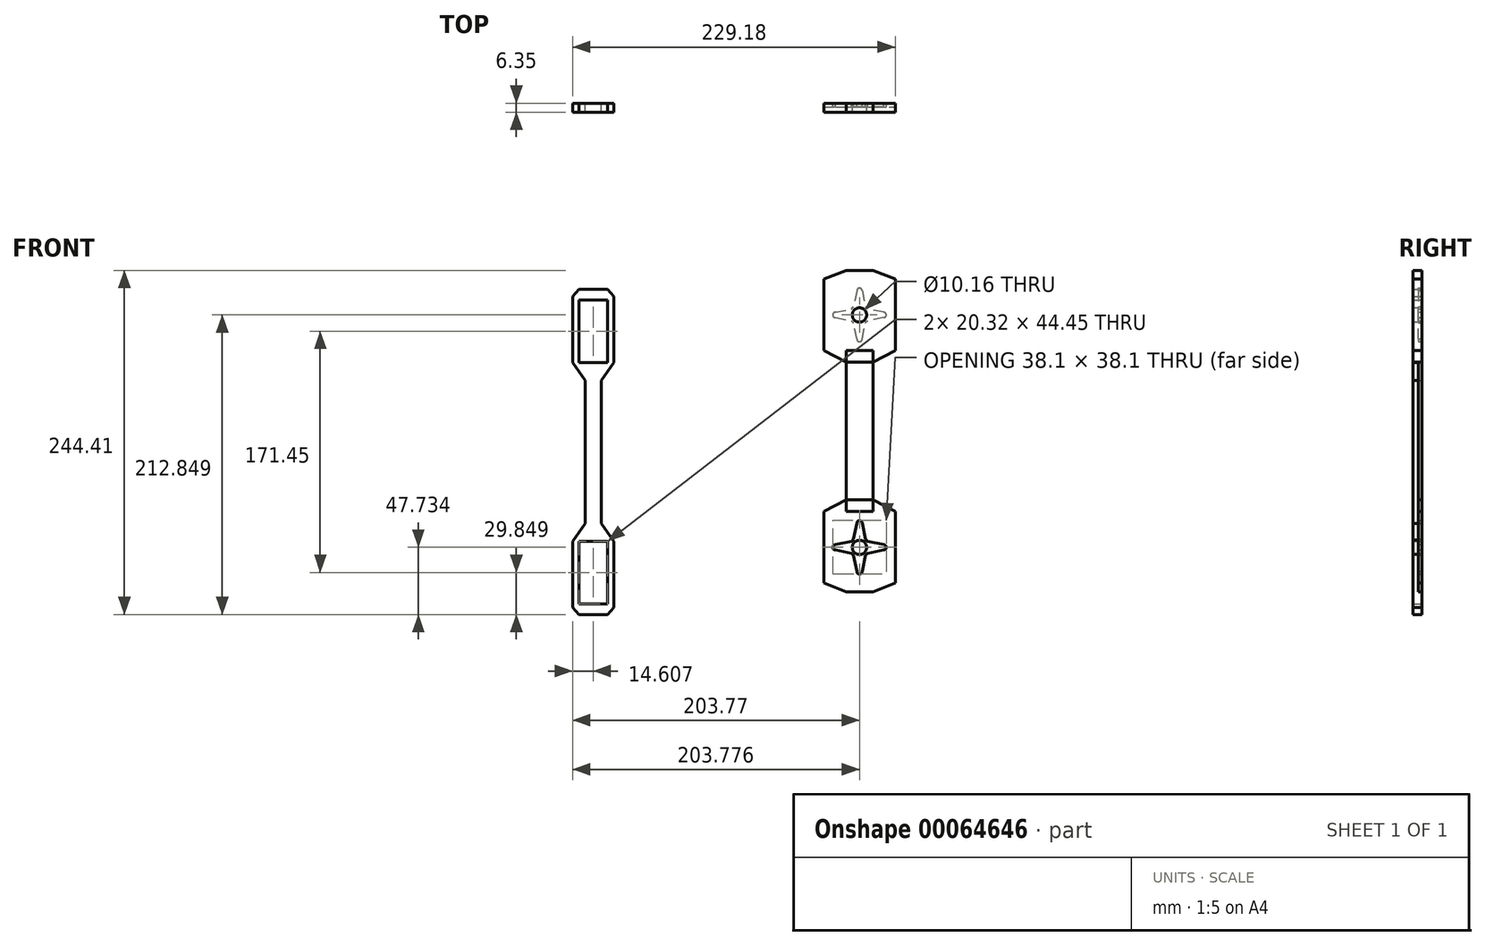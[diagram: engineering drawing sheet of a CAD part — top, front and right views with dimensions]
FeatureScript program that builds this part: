
annotation { "Feature Type Name" : "Feature", "Feature Type Description" : "" }
export const myFeature = defineFeature(function(context is Context, id is Id, definition is map)
    precondition{}
    {
        {
            var Q0;
            Q0=qCreatedBy(makeId("Front.planeOp"),FACE);
            var sketch = newSketch(context, id + "F0", { "sketchPlane" : qUnion([Q0])});
            skLineSegment(sketch, "E0.bottom", {"start": v(-81.1, 17.43) * mm, "end": v(-69.67, 17.43) * mm});
            skLineSegment(sketch, "E0.top", {"start": v(-81.1, -46.07) * mm, "end": v(-69.67, -46.07) * mm});
            skLineSegment(sketch, "E0.left", {"start": v(-81.1, 17.43) * mm, "end": v(-81.1, -46.07) * mm});
            skLineSegment(sketch, "E0.right", {"start": v(-69.67, 17.43) * mm, "end": v(-69.67, -46.07) * mm});
            skLineSegment(sketch, "E1.bottom", {"start": v(-89.99, 17.43) * mm, "end": v(-60.78, 17.43) * mm});
            skLineSegment(sketch, "E1.top", {"start": v(-89.99, 64.42) * mm, "end": v(-60.78, 64.42) * mm});
            skLineSegment(sketch, "E1.left", {"start": v(-89.99, 17.43) * mm, "end": v(-89.99, 64.42) * mm});
            skLineSegment(sketch, "E1.right", {"start": v(-60.78, 17.43) * mm, "end": v(-60.78, 64.42) * mm});
            skLineSegment(sketch, "E2", {"start": v(-81.1, 4.73) * mm, "end": v(-89.99, 17.43) * mm});
            skLineSegment(sketch, "E3", {"start": v(-69.67, 4.73) * mm, "end": v(-60.78, 17.43) * mm});
            skLineSegment(sketch, "E4.bottom", {"start": v(-85.54, 17.43) * mm, "end": v(-65.22, 17.43) * mm});
            skLineSegment(sketch, "E4.top", {"start": v(-85.54, 61.88) * mm, "end": v(-65.22, 61.88) * mm});
            skLineSegment(sketch, "E4.left", {"start": v(-85.54, 17.43) * mm, "end": v(-85.54, 61.88) * mm});
            skLineSegment(sketch, "E4.right", {"start": v(-65.22, 17.43) * mm, "end": v(-65.22, 61.88) * mm});
            skLineSegment(sketch, "E5.MirrorCS", {"start": v(-81.1, -109.57) * mm, "end": v(-69.67, -109.57) * mm});
            skLineSegment(sketch, "E6.MirrorCS", {"start": v(-81.1, -109.57) * mm, "end": v(-81.1, -46.07) * mm});
            skLineSegment(sketch, "E7.MirrorCS", {"start": v(-69.67, -109.57) * mm, "end": v(-69.67, -46.07) * mm});
            skLineSegment(sketch, "E8.MirrorCS", {"start": v(-89.99, -109.57) * mm, "end": v(-60.78, -109.57) * mm});
            skLineSegment(sketch, "E9.MirrorCS", {"start": v(-89.99, -156.56) * mm, "end": v(-60.78, -156.56) * mm});
            skLineSegment(sketch, "E10.MirrorCS", {"start": v(-89.99, -109.57) * mm, "end": v(-89.99, -156.56) * mm});
            skLineSegment(sketch, "E11.MirrorCS", {"start": v(-60.78, -109.57) * mm, "end": v(-60.78, -156.56) * mm});
            skLineSegment(sketch, "E12.MirrorCS", {"start": v(-81.1, -96.87) * mm, "end": v(-89.99, -109.57) * mm});
            skLineSegment(sketch, "E13.MirrorCS", {"start": v(-69.67, -96.87) * mm, "end": v(-60.78, -109.57) * mm});
            skLineSegment(sketch, "E14.MirrorCS", {"start": v(-65.22, -109.57) * mm, "end": v(-65.22, -154.02) * mm});
            skLineSegment(sketch, "E15.MirrorCS", {"start": v(-85.54, -109.57) * mm, "end": v(-85.54, -154.02) * mm});
            skLineSegment(sketch, "E16.MirrorCS", {"start": v(-85.54, -154.02) * mm, "end": v(-65.22, -154.02) * mm});
            skLineSegment(sketch, "E17.MirrorCS", {"start": v(-85.54, -109.57) * mm, "end": v(-65.22, -109.57) * mm});
            skLineSegment(sketch, "E18", {"start": v(-89.99, 64.42) * mm, "end": v(-85.54, 69.5) * mm});
            skLineSegment(sketch, "E19", {"start": v(-85.54, 69.5) * mm, "end": v(-65.22, 69.5) * mm});
            skLineSegment(sketch, "E20", {"start": v(-65.22, 69.5) * mm, "end": v(-60.78, 64.42) * mm});
            skLineSegment(sketch, "E21.MirrorCS", {"start": v(-85.54, -161.64) * mm, "end": v(-65.22, -161.64) * mm});
            skLineSegment(sketch, "E22.MirrorCS", {"start": v(-89.99, -156.56) * mm, "end": v(-85.54, -161.64) * mm});
            skLineSegment(sketch, "E23.MirrorCS", {"start": v(-65.22, -161.64) * mm, "end": v(-60.78, -156.56) * mm});
            skSolve(sketch);
        }
        {
            var Q0;
            Q0=makeQuery(id+"F0.imprint","IMPRINT",FACE,{"disambiguationData":[TD([[makeQuery(id+"F0.imprint","IMPRINT",EDGE,{"derivedFrom":sQuery(id+"F0.wireOp",EDGE,"E1.top")}),-1.0]])]});
            var Q1;
            {var subQ3=sQuery(id+"F0.wireOp",EDGE,"E2");Q1=makeQuery(id+"F0.imprint","IMPRINT",FACE,{"disambiguationData":[TD([[makeQuery(id+"F0.imprint","IMPRINT",EDGE,{"derivedFrom":subQ3}),-1.0]])]});}
            var Q2;
            {var subQ5=sQuery(id+"F0.wireOp",EDGE,"E0.top");Q2=makeQuery(id+"F0.imprint","IMPRINT",FACE,{"disambiguationData":[TD([[makeQuery(id+"F0.imprint","IMPRINT",EDGE,{"derivedFrom":subQ5}),1.0]])]});}
            var Q3;
            {var subQ3=sQuery(id+"F0.wireOp",EDGE,"E3");Q3=makeQuery(id+"F0.imprint","IMPRINT",FACE,{"disambiguationData":[TD([[makeQuery(id+"F0.imprint","IMPRINT",EDGE,{"derivedFrom":subQ3}),1.0]])]});}
            var Q4;
            {var subQ5=sQuery(id+"F0.wireOp",EDGE,"E0.top");Q4=makeQuery(id+"F0.imprint","IMPRINT",FACE,{"disambiguationData":[TD([[makeQuery(id+"F0.imprint","IMPRINT",EDGE,{"derivedFrom":subQ5}),-1.0]])]});}
            var Q5;
            {var subQ3=sQuery(id+"F0.wireOp",EDGE,"E12.MirrorCS");Q5=makeQuery(id+"F0.imprint","IMPRINT",FACE,{"disambiguationData":[TD([[makeQuery(id+"F0.imprint","IMPRINT",EDGE,{"derivedFrom":subQ3}),1.0]])]});}
            var Q6;
            {var subQ3=sQuery(id+"F0.wireOp",EDGE,"E13.MirrorCS");Q6=makeQuery(id+"F0.imprint","IMPRINT",FACE,{"disambiguationData":[TD([[makeQuery(id+"F0.imprint","IMPRINT",EDGE,{"derivedFrom":subQ3}),-1.0]])]});}
            var Q7;
            Q7=makeQuery(id+"F0.imprint","IMPRINT",FACE,{"disambiguationData":[TD([[makeQuery(id+"F0.imprint","IMPRINT",EDGE,{"derivedFrom":sQuery(id+"F0.wireOp",EDGE,"E9.MirrorCS")}),1.0]])]});
            var Q8;
            Q8=makeQuery(id+"F0.imprint","IMPRINT",FACE,{"disambiguationData":[TD([[makeQuery(id+"F0.imprint","IMPRINT",EDGE,{"derivedFrom":sQuery(id+"F0.wireOp",EDGE,"E1.top")}),1.0]])]});
            var Q9;
            Q9=makeQuery(id+"F0.imprint","IMPRINT",FACE,{"disambiguationData":[TD([[makeQuery(id+"F0.imprint","IMPRINT",EDGE,{"derivedFrom":sQuery(id+"F0.wireOp",EDGE,"E9.MirrorCS")}),-1.0]])]});
            extrude(context, id + "F1", {"entities" : qUnion([Q0, Q1, Q2, Q3, Q4, Q5, Q6, Q7, Q8, Q9]), "depth" : 6.35 * mm});
        }
        {
            var Q0;
            Q0=qCreatedBy(makeId("Front.planeOp"),FACE);
            var sketch = newSketch(context, id + "F2", { "sketchPlane" : qUnion([Q0])});
            skLineSegment(sketch, "E24.bottom", {"start": v(88.39, 76.6) * mm, "end": v(139.19, 76.6) * mm});
            skLineSegment(sketch, "E24.top", {"start": v(88.39, 25.8) * mm, "end": v(139.19, 25.8) * mm});
            skLineSegment(sketch, "E24.left", {"start": v(88.39, 76.6) * mm, "end": v(88.39, 25.8) * mm});
            skLineSegment(sketch, "E24.right", {"start": v(139.19, 76.6) * mm, "end": v(139.19, 25.8) * mm});
            skLineSegment(sketch, "E25.bottom", {"start": v(104.26, -31.36) * mm, "end": v(123.31, -31.36) * mm});
            skLineSegment(sketch, "E25.top", {"start": v(104.26, 25.8) * mm, "end": v(123.31, 25.8) * mm});
            skLineSegment(sketch, "E25.left", {"start": v(104.26, -31.36) * mm, "end": v(104.26, 25.8) * mm});
            skLineSegment(sketch, "E25.right", {"start": v(123.31, -31.36) * mm, "end": v(123.31, 25.8) * mm});
            skLineSegment(sketch, "E26", {"start": v(88.39, 25.8) * mm, "end": v(104.26, 17.53) * mm});
            skLineSegment(sketch, "E27", {"start": v(104.26, 17.53) * mm, "end": v(123.31, 17.53) * mm});
            skLineSegment(sketch, "E28", {"start": v(123.31, 17.53) * mm, "end": v(139.19, 25.8) * mm});
            skLineSegment(sketch, "E29", {"start": v(88.39, 76.6) * mm, "end": v(104.26, 82.77) * mm});
            skLineSegment(sketch, "E30", {"start": v(104.26, 82.77) * mm, "end": v(123.31, 82.77) * mm});
            skLineSegment(sketch, "E31", {"start": v(123.31, 82.77) * mm, "end": v(139.19, 76.6) * mm});
            skLineSegment(sketch, "E32", {"start": v(113.79, 51.2) * mm, "end": v(113.79, 70.24) * mm});
            skPoint(sketch, "E32.startSnap0", {"position": v(113.79, 76.6) * mm});
            skPoint(sketch, "E32.startSnap1", {"position": v(88.39, 51.2) * mm});
            skCircle(sketch, "E33", {"center": v(113.79, 68.34) * mm, "radius": 1.9 * mm});
            skCircle(sketch, "E34", {"center": v(113.79, 51.2) * mm, "radius": 4.86 * mm});
            skLineSegment(sketch, "E35", {"start": v(113.79, 51.2) * mm, "end": v(110.35, 54.63) * mm});
            skLineSegment(sketch, "E36", {"start": v(110.35, 54.63) * mm, "end": v(111.88, 68.34) * mm});
            skLineSegment(sketch, "E37.MirrorCS", {"start": v(117.23, 54.63) * mm, "end": v(115.7, 68.34) * mm});
            skLineSegment(sketch, "E38", {"start": v(111.88, 68.34) * mm, "end": v(109.47, 56.89) * mm});
            skLineSegment(sketch, "E39.MirrorCS", {"start": v(115.7, 68.34) * mm, "end": v(118.1, 56.89) * mm});
            skLineSegment(sketch, "E40.1.0", {"start": v(96.64, 53.1) * mm, "end": v(108.1, 55.51) * mm});
            skLineSegment(sketch, "E40.1.1", {"start": v(96.64, 49.29) * mm, "end": v(108.1, 46.88) * mm});
            skCircle(sketch, "E40.1.2", {"center": v(96.64, 51.2) * mm, "radius": 1.9 * mm});
            skLineSegment(sketch, "E40.1.3", {"start": v(113.79, 51.2) * mm, "end": v(94.74, 51.2) * mm});
            skLineSegment(sketch, "E40.2.0", {"start": v(111.88, 34.05) * mm, "end": v(109.47, 45.5) * mm});
            skLineSegment(sketch, "E40.2.1", {"start": v(115.7, 34.05) * mm, "end": v(118.1, 45.5) * mm});
            skCircle(sketch, "E40.2.2", {"center": v(113.79, 34.05) * mm, "radius": 1.9 * mm});
            skLineSegment(sketch, "E40.2.3", {"start": v(113.79, 51.2) * mm, "end": v(113.79, 32.14) * mm});
            skLineSegment(sketch, "E40.3.0", {"start": v(130.93, 49.29) * mm, "end": v(119.48, 46.88) * mm});
            skLineSegment(sketch, "E40.3.1", {"start": v(130.93, 53.1) * mm, "end": v(119.48, 55.51) * mm});
            skCircle(sketch, "E40.3.2", {"center": v(130.93, 51.2) * mm, "radius": 1.9 * mm});
            skLineSegment(sketch, "E40.3.3", {"start": v(113.79, 51.2) * mm, "end": v(132.84, 51.2) * mm});
            skLineSegment(sketch, "E41", {"start": v(108.1, 55.51) * mm, "end": v(109.47, 56.89) * mm});
            skLineSegment(sketch, "E42", {"start": v(118.1, 56.89) * mm, "end": v(119.48, 55.51) * mm});
            skLineSegment(sketch, "E43", {"start": v(119.48, 46.88) * mm, "end": v(118.1, 45.5) * mm});
            skLineSegment(sketch, "E44", {"start": v(109.47, 45.5) * mm, "end": v(108.1, 46.88) * mm});
            skLineSegment(sketch, "E45.MirrorCS", {"start": v(113.79, -113.9) * mm, "end": v(110.35, -117.34) * mm});
            skLineSegment(sketch, "E46.MirrorCS", {"start": v(108.1, -118.22) * mm, "end": v(109.47, -119.6) * mm});
            skCircle(sketch, "E47.MirrorC", {"center": v(113.79, -131.05) * mm, "radius": 1.9 * mm});
            skCircle(sketch, "E48.MirrorC", {"center": v(130.93, -113.9) * mm, "radius": 1.9 * mm});
            skLineSegment(sketch, "E49.MirrorCS", {"start": v(109.47, -108.21) * mm, "end": v(108.1, -109.59) * mm});
            skCircle(sketch, "E50.MirrorC", {"center": v(113.79, -113.9) * mm, "radius": 4.86 * mm});
            skLineSegment(sketch, "E51.MirrorCS", {"start": v(111.88, -131.05) * mm, "end": v(109.47, -119.6) * mm});
            skCircle(sketch, "E52.MirrorC", {"center": v(113.79, -96.76) * mm, "radius": 1.9 * mm});
            skLineSegment(sketch, "E53.MirrorCS", {"start": v(118.1, -119.6) * mm, "end": v(119.48, -118.22) * mm});
            skLineSegment(sketch, "E54.MirrorCS", {"start": v(119.48, -109.59) * mm, "end": v(118.1, -108.21) * mm});
            skLineSegment(sketch, "E55.MirrorCS", {"start": v(115.7, -131.05) * mm, "end": v(118.1, -119.6) * mm});
            skLineSegment(sketch, "E56.MirrorCS", {"start": v(113.79, -113.9) * mm, "end": v(113.79, -132.96) * mm});
            skLineSegment(sketch, "E57.MirrorCS", {"start": v(110.35, -117.34) * mm, "end": v(111.88, -131.05) * mm});
            skCircle(sketch, "E58.MirrorC", {"center": v(96.64, -113.9) * mm, "radius": 1.9 * mm});
            skLineSegment(sketch, "E59.MirrorCS", {"start": v(88.39, -88.5) * mm, "end": v(104.26, -80.24) * mm});
            skLineSegment(sketch, "E60.MirrorCS", {"start": v(115.7, -96.76) * mm, "end": v(118.1, -108.21) * mm});
            skLineSegment(sketch, "E61.MirrorCS", {"start": v(96.64, -112) * mm, "end": v(108.1, -109.59) * mm});
            skLineSegment(sketch, "E62.MirrorCS", {"start": v(123.31, -31.36) * mm, "end": v(123.31, -88.5) * mm});
            skLineSegment(sketch, "E63.MirrorCS", {"start": v(88.39, -139.3) * mm, "end": v(88.39, -88.5) * mm});
            skLineSegment(sketch, "E64.MirrorCS", {"start": v(130.93, -112) * mm, "end": v(119.48, -109.59) * mm});
            skLineSegment(sketch, "E65.MirrorCS", {"start": v(88.39, -139.3) * mm, "end": v(139.19, -139.3) * mm});
            skLineSegment(sketch, "E66.MirrorCS", {"start": v(104.26, -145.48) * mm, "end": v(123.31, -145.48) * mm});
            skLineSegment(sketch, "E67.MirrorCS", {"start": v(88.39, -88.5) * mm, "end": v(139.19, -88.5) * mm});
            skLineSegment(sketch, "E68.MirrorCS", {"start": v(113.79, -113.9) * mm, "end": v(94.74, -113.9) * mm});
            skLineSegment(sketch, "E69.MirrorCS", {"start": v(104.26, -31.36) * mm, "end": v(104.26, -88.5) * mm});
            skPoint(sketch, "E70.MirrorP", {"position": v(113.79, -139.3) * mm});
            skLineSegment(sketch, "E71.MirrorCS", {"start": v(113.79, -113.9) * mm, "end": v(132.84, -113.9) * mm});
            skLineSegment(sketch, "E72.MirrorCS", {"start": v(96.64, -115.81) * mm, "end": v(108.1, -118.22) * mm});
            skLineSegment(sketch, "E73.MirrorCS", {"start": v(130.93, -115.81) * mm, "end": v(119.48, -118.22) * mm});
            skPoint(sketch, "E74.MirrorP", {"position": v(88.39, -113.9) * mm});
            skLineSegment(sketch, "E75.MirrorCS", {"start": v(111.88, -96.76) * mm, "end": v(109.47, -108.21) * mm});
            skLineSegment(sketch, "E76.MirrorCS", {"start": v(113.79, -113.9) * mm, "end": v(113.79, -94.86) * mm});
            skLineSegment(sketch, "E77.MirrorCS", {"start": v(117.23, -117.34) * mm, "end": v(115.7, -131.05) * mm});
            skLineSegment(sketch, "E78.MirrorCS", {"start": v(139.19, -139.3) * mm, "end": v(139.19, -88.5) * mm});
            skLineSegment(sketch, "E79.MirrorCS", {"start": v(88.39, -139.3) * mm, "end": v(104.26, -145.48) * mm});
            skLineSegment(sketch, "E80.MirrorCS", {"start": v(123.31, -80.24) * mm, "end": v(139.19, -88.5) * mm});
            skLineSegment(sketch, "E81.MirrorCS", {"start": v(123.31, -145.48) * mm, "end": v(139.19, -139.3) * mm});
            skLineSegment(sketch, "E82.MirrorCS", {"start": v(104.26, -88.5) * mm, "end": v(123.31, -88.5) * mm});
            skLineSegment(sketch, "E83.MirrorCS", {"start": v(104.26, -80.24) * mm, "end": v(123.31, -80.24) * mm});
            skSolve(sketch);
        }
        {
            var Q0;
            Q0=makeQuery(id+"F2.imprint","IMPRINT",FACE,{"disambiguationData":[TD([[makeQuery(id+"F2.imprint","IMPRINT",EDGE,{"derivedFrom":sQuery(id+"F2.wireOp",EDGE,"E46.MirrorCS")}),-1.0]])]});
            var Q1;
            Q1=makeQuery(id+"F2.imprint","IMPRINT",FACE,{"disambiguationData":[TD([[makeQuery(id+"F2.imprint","IMPRINT",EDGE,{"derivedFrom":sQuery(id+"F2.wireOp",EDGE,"E65.MirrorCS")}),-1.0]])]});
            var Q2;
            {var subQ0=sQuery(id+"F2.wireOp",EDGE,"E59.MirrorCS");Q2=makeQuery(id+"F2.imprint","IMPRINT",FACE,{"disambiguationData":[TD([[makeQuery(id+"F2.imprint","IMPRINT",EDGE,{"derivedFrom":subQ0}),-1.0]])]});}
            var Q3;
            {var subQ0=sQuery(id+"F2.wireOp",EDGE,"E82.MirrorCS");Q3=makeQuery(id+"F2.imprint","IMPRINT",FACE,{"disambiguationData":[TD([[makeQuery(id+"F2.imprint","IMPRINT",EDGE,{"derivedFrom":subQ0}),1.0]])]});}
            var Q4;
            {var subQ3=sQuery(id+"F2.wireOp",EDGE,"E80.MirrorCS");Q4=makeQuery(id+"F2.imprint","IMPRINT",FACE,{"disambiguationData":[TD([[makeQuery(id+"F2.imprint","IMPRINT",EDGE,{"derivedFrom":subQ3}),-1.0]])]});}
            var Q5;
            {var subQ0=sQuery(id+"F2.wireOp",EDGE,"E25.bottom");Q5=makeQuery(id+"F2.imprint","IMPRINT",FACE,{"disambiguationData":[TD([[makeQuery(id+"F2.imprint","IMPRINT",EDGE,{"derivedFrom":subQ0}),-1.0]])]});}
            var Q6;
            {var subQ0=sQuery(id+"F2.wireOp",EDGE,"E25.bottom");Q6=makeQuery(id+"F2.imprint","IMPRINT",FACE,{"disambiguationData":[TD([[makeQuery(id+"F2.imprint","IMPRINT",EDGE,{"derivedFrom":subQ0}),1.0]])]});}
            var Q7;
            Q7=makeQuery(id+"F2.imprint","IMPRINT",FACE,{"disambiguationData":[TD([[makeQuery(id+"F2.imprint","IMPRINT",EDGE,{"derivedFrom":sQuery(id+"F2.wireOp",EDGE,"E24.bottom")}),-1.0]])]});
            var Q8;
            {var subQ0=sQuery(id+"F2.wireOp",EDGE,"E26");Q8=makeQuery(id+"F2.imprint","IMPRINT",FACE,{"disambiguationData":[TD([[makeQuery(id+"F2.imprint","IMPRINT",EDGE,{"derivedFrom":subQ0}),1.0]])]});}
            var Q9;
            {var subQ0=sQuery(id+"F2.wireOp",EDGE,"E25.top");Q9=makeQuery(id+"F2.imprint","IMPRINT",FACE,{"disambiguationData":[TD([[makeQuery(id+"F2.imprint","IMPRINT",EDGE,{"derivedFrom":subQ0}),-1.0]])]});}
            var Q10;
            {var subQ0=sQuery(id+"F2.wireOp",EDGE,"E28");Q10=makeQuery(id+"F2.imprint","IMPRINT",FACE,{"disambiguationData":[TD([[makeQuery(id+"F2.imprint","IMPRINT",EDGE,{"derivedFrom":subQ0}),1.0]])]});}
            var Q11;
            Q11=makeQuery(id+"F2.imprint","IMPRINT",FACE,{"disambiguationData":[TD([[makeQuery(id+"F2.imprint","IMPRINT",EDGE,{"derivedFrom":sQuery(id+"F2.wireOp",EDGE,"E24.bottom")}),1.0]])]});
            var Q12;
            Q12 = qSketchRegion(id + "F4", true);
            extrude(context, id + "F3", {"entities" : qUnion([Q0, Q1, Q2, Q3, Q4, Q5, Q6, Q7, Q8, Q9, Q10, Q11, Q12]), "depth" : 2.54 * mm});
        }
        {
            var Q0;
            Q0=makeQuery(id+"F3.opExtrude","CAP_FACE",FACE,{"disambiguationData":[OSD([sQuery(id+"F2.wireOp",EDGE,"E24.left"),sQuery(id+"F2.wireOp",EDGE,"E24.right"),sQuery(id+"F2.wireOp",EDGE,"E25.left"),sQuery(id+"F2.wireOp",EDGE,"E25.right"),sQuery(id+"F2.wireOp",EDGE,"E26"),sQuery(id+"F2.wireOp",EDGE,"E28"),sQuery(id+"F2.wireOp",EDGE,"E29"),sQuery(id+"F2.wireOp",EDGE,"E30"),sQuery(id+"F2.wireOp",EDGE,"E31"),sQuery(id+"F2.wireOp",EDGE,"E33"),sQuery(id+"F2.wireOp",EDGE,"E38"),sQuery(id+"F2.wireOp",EDGE,"E39.MirrorCS"),sQuery(id+"F2.wireOp",EDGE,"E40.1.0"),sQuery(id+"F2.wireOp",EDGE,"E40.1.1"),sQuery(id+"F2.wireOp",EDGE,"E40.1.2"),sQuery(id+"F2.wireOp",EDGE,"E40.2.0"),sQuery(id+"F2.wireOp",EDGE,"E40.2.1"),sQuery(id+"F2.wireOp",EDGE,"E40.2.2"),sQuery(id+"F2.wireOp",EDGE,"E40.3.0"),sQuery(id+"F2.wireOp",EDGE,"E40.3.1"),sQuery(id+"F2.wireOp",EDGE,"E40.3.2"),sQuery(id+"F2.wireOp",EDGE,"E41"),sQuery(id+"F2.wireOp",EDGE,"E42"),sQuery(id+"F2.wireOp",EDGE,"E43"),sQuery(id+"F2.wireOp",EDGE,"E44"),sQuery(id+"F2.wireOp",EDGE,"E46.MirrorCS"),sQuery(id+"F2.wireOp",EDGE,"E47.MirrorC"),sQuery(id+"F2.wireOp",EDGE,"E48.MirrorC"),sQuery(id+"F2.wireOp",EDGE,"E49.MirrorCS"),sQuery(id+"F2.wireOp",EDGE,"E51.MirrorCS"),sQuery(id+"F2.wireOp",EDGE,"E52.MirrorC"),sQuery(id+"F2.wireOp",EDGE,"E53.MirrorCS"),sQuery(id+"F2.wireOp",EDGE,"E54.MirrorCS"),sQuery(id+"F2.wireOp",EDGE,"E55.MirrorCS"),sQuery(id+"F2.wireOp",EDGE,"E58.MirrorC"),sQuery(id+"F2.wireOp",EDGE,"E59.MirrorCS"),sQuery(id+"F2.wireOp",EDGE,"E60.MirrorCS"),sQuery(id+"F2.wireOp",EDGE,"E61.MirrorCS"),sQuery(id+"F2.wireOp",EDGE,"E62.MirrorCS"),sQuery(id+"F2.wireOp",EDGE,"E63.MirrorCS"),sQuery(id+"F2.wireOp",EDGE,"E64.MirrorCS"),sQuery(id+"F2.wireOp",EDGE,"E66.MirrorCS"),sQuery(id+"F2.wireOp",EDGE,"E69.MirrorCS"),sQuery(id+"F2.wireOp",EDGE,"E72.MirrorCS"),sQuery(id+"F2.wireOp",EDGE,"E73.MirrorCS"),sQuery(id+"F2.wireOp",EDGE,"E75.MirrorCS"),sQuery(id+"F2.wireOp",EDGE,"E78.MirrorCS"),sQuery(id+"F2.wireOp",EDGE,"E79.MirrorCS"),sQuery(id+"F2.wireOp",EDGE,"E80.MirrorCS"),sQuery(id+"F2.wireOp",EDGE,"E81.MirrorCS")])],"isStart":false});
            var sketch = newSketch(context, id + "F4", { "sketchPlane" : qUnion([Q0])});
            skCircle(sketch, "E84", {"center": v(113.78, 51.2) * mm, "radius": 5.08 * mm});
            skLineSegment(sketch, "E85", {"start": v(123.31, -31.36) * mm, "end": v(104.26, -31.36) * mm});
            skCircle(sketch, "E86.MirrorC", {"center": v(113.78, -113.92) * mm, "radius": 5.08 * mm});
            skSolve(sketch);
        }
        {
            var Q0;
            Q0=makeQuery(id+"F4.imprint","IMPRINT",FACE,{"disambiguationData":[TD([[makeQuery(id+"F4.imprint","IMPRINT",EDGE,{"derivedFrom":makeQuery(id+"F3.opExtrude","CAP_EDGE",EDGE,{"disambiguationData":[OSD([sQuery(id+"F2.wireOp",EDGE,"E24.left")])],"isStart":false})}),1.0]])]});
            var Q1;
            Q1=makeQuery(id+"F4.imprint","IMPRINT",FACE,{"disambiguationData":[TD([[makeQuery(id+"F4.imprint","IMPRINT",EDGE,{"derivedFrom":sQuery(id+"F4.wireOp",EDGE,"E84")}),-1.0]])]});
            extrude(context, id + "F5", {"entities" : qUnion([Q0, Q1]), "operationType" : NewBodyOperationType.ADD, "depth" : 3.8 * mm});
        }
        {
            var Q0;
            Q0=makeQuery(id+"F5.opExtrude","CAP_FACE",FACE,{"disambiguationData":[OSD([sQuery(id+"F2.wireOp",EDGE,"E24.left"),sQuery(id+"F2.wireOp",EDGE,"E24.right"),sQuery(id+"F2.wireOp",EDGE,"E25.left"),sQuery(id+"F2.wireOp",EDGE,"E25.right"),sQuery(id+"F2.wireOp",EDGE,"E26"),sQuery(id+"F2.wireOp",EDGE,"E28"),sQuery(id+"F2.wireOp",EDGE,"E29"),sQuery(id+"F2.wireOp",EDGE,"E30"),sQuery(id+"F2.wireOp",EDGE,"E31"),sQuery(id+"F2.wireOp",EDGE,"E46.MirrorCS"),sQuery(id+"F2.wireOp",EDGE,"E47.MirrorC"),sQuery(id+"F2.wireOp",EDGE,"E48.MirrorC"),sQuery(id+"F2.wireOp",EDGE,"E49.MirrorCS"),sQuery(id+"F2.wireOp",EDGE,"E51.MirrorCS"),sQuery(id+"F2.wireOp",EDGE,"E52.MirrorC"),sQuery(id+"F2.wireOp",EDGE,"E53.MirrorCS"),sQuery(id+"F2.wireOp",EDGE,"E54.MirrorCS"),sQuery(id+"F2.wireOp",EDGE,"E55.MirrorCS"),sQuery(id+"F2.wireOp",EDGE,"E58.MirrorC"),sQuery(id+"F2.wireOp",EDGE,"E59.MirrorCS"),sQuery(id+"F2.wireOp",EDGE,"E60.MirrorCS"),sQuery(id+"F2.wireOp",EDGE,"E61.MirrorCS"),sQuery(id+"F2.wireOp",EDGE,"E62.MirrorCS"),sQuery(id+"F2.wireOp",EDGE,"E63.MirrorCS"),sQuery(id+"F2.wireOp",EDGE,"E64.MirrorCS"),sQuery(id+"F2.wireOp",EDGE,"E66.MirrorCS"),sQuery(id+"F2.wireOp",EDGE,"E69.MirrorCS"),sQuery(id+"F2.wireOp",EDGE,"E72.MirrorCS"),sQuery(id+"F2.wireOp",EDGE,"E73.MirrorCS"),sQuery(id+"F2.wireOp",EDGE,"E75.MirrorCS"),sQuery(id+"F2.wireOp",EDGE,"E78.MirrorCS"),sQuery(id+"F2.wireOp",EDGE,"E79.MirrorCS"),sQuery(id+"F2.wireOp",EDGE,"E80.MirrorCS"),sQuery(id+"F2.wireOp",EDGE,"E81.MirrorCS"),sQuery(id+"F4.wireOp",EDGE,"E84")])],"isStart":false});
            var sketch = newSketch(context, id + "F6", { "sketchPlane" : qUnion([Q0])});
            skLineSegment(sketch, "E87", {"start": v(104.26, 17.53) * mm, "end": v(123.31, 17.53) * mm});
            skSolve(sketch);
        }
        {
            var Q0;
            Q0=makeQuery(id+"F1.opExtrude","CAP_FACE",FACE,{"disambiguationData":[OSD([sQuery(id+"F0.wireOp",EDGE,"E0.left"),sQuery(id+"F0.wireOp",EDGE,"E0.right"),sQuery(id+"F0.wireOp",EDGE,"E1.left"),sQuery(id+"F0.wireOp",EDGE,"E1.right"),sQuery(id+"F0.wireOp",EDGE,"E2"),sQuery(id+"F0.wireOp",EDGE,"E3"),sQuery(id+"F0.wireOp",EDGE,"E4.bottom"),sQuery(id+"F0.wireOp",EDGE,"E4.top"),sQuery(id+"F0.wireOp",EDGE,"E4.left"),sQuery(id+"F0.wireOp",EDGE,"E4.right"),sQuery(id+"F0.wireOp",EDGE,"E6.MirrorCS"),sQuery(id+"F0.wireOp",EDGE,"E7.MirrorCS"),sQuery(id+"F0.wireOp",EDGE,"E10.MirrorCS"),sQuery(id+"F0.wireOp",EDGE,"E11.MirrorCS"),sQuery(id+"F0.wireOp",EDGE,"E12.MirrorCS"),sQuery(id+"F0.wireOp",EDGE,"E13.MirrorCS"),sQuery(id+"F0.wireOp",EDGE,"E14.MirrorCS"),sQuery(id+"F0.wireOp",EDGE,"E15.MirrorCS"),sQuery(id+"F0.wireOp",EDGE,"E16.MirrorCS"),sQuery(id+"F0.wireOp",EDGE,"E17.MirrorCS"),sQuery(id+"F0.wireOp",EDGE,"E18"),sQuery(id+"F0.wireOp",EDGE,"E19"),sQuery(id+"F0.wireOp",EDGE,"E20"),sQuery(id+"F0.wireOp",EDGE,"E21.MirrorCS"),sQuery(id+"F0.wireOp",EDGE,"E22.MirrorCS"),sQuery(id+"F0.wireOp",EDGE,"E23.MirrorCS")])],"isStart":true});
            var sketch = newSketch(context, id + "F7", { "sketchPlane" : qUnion([Q0])});
            skLineSegment(sketch, "E88", {"start": v(69.67, 4.73) * mm, "end": v(81.1, 4.73) * mm});
            skSolve(sketch);
        }
        {
            var Q0;
            Q0=makeQuery(id+"F4.imprint","IMPRINT",FACE,{"disambiguationData":[TD([[makeQuery(id+"F4.imprint","IMPRINT",EDGE,{"derivedFrom":sQuery(id+"F4.wireOp",EDGE,"E86.MirrorC")}),1.0]])]});
            var Q1;
            {var subQ1=sQuery(id+"F4.wireOp",EDGE,"E85");Q1=makeQuery(id+"F4.imprint","IMPRINT",FACE,{"disambiguationData":[TD([[makeQuery(id+"F4.imprint","IMPRINT",EDGE,{"derivedFrom":subQ1}),1.0]])]});}
            extrude(context, id + "F8", {"entities" : qUnion([Q0, Q1]), "operationType" : NewBodyOperationType.ADD, "depth" : 3.8 * mm});
        }
    });
